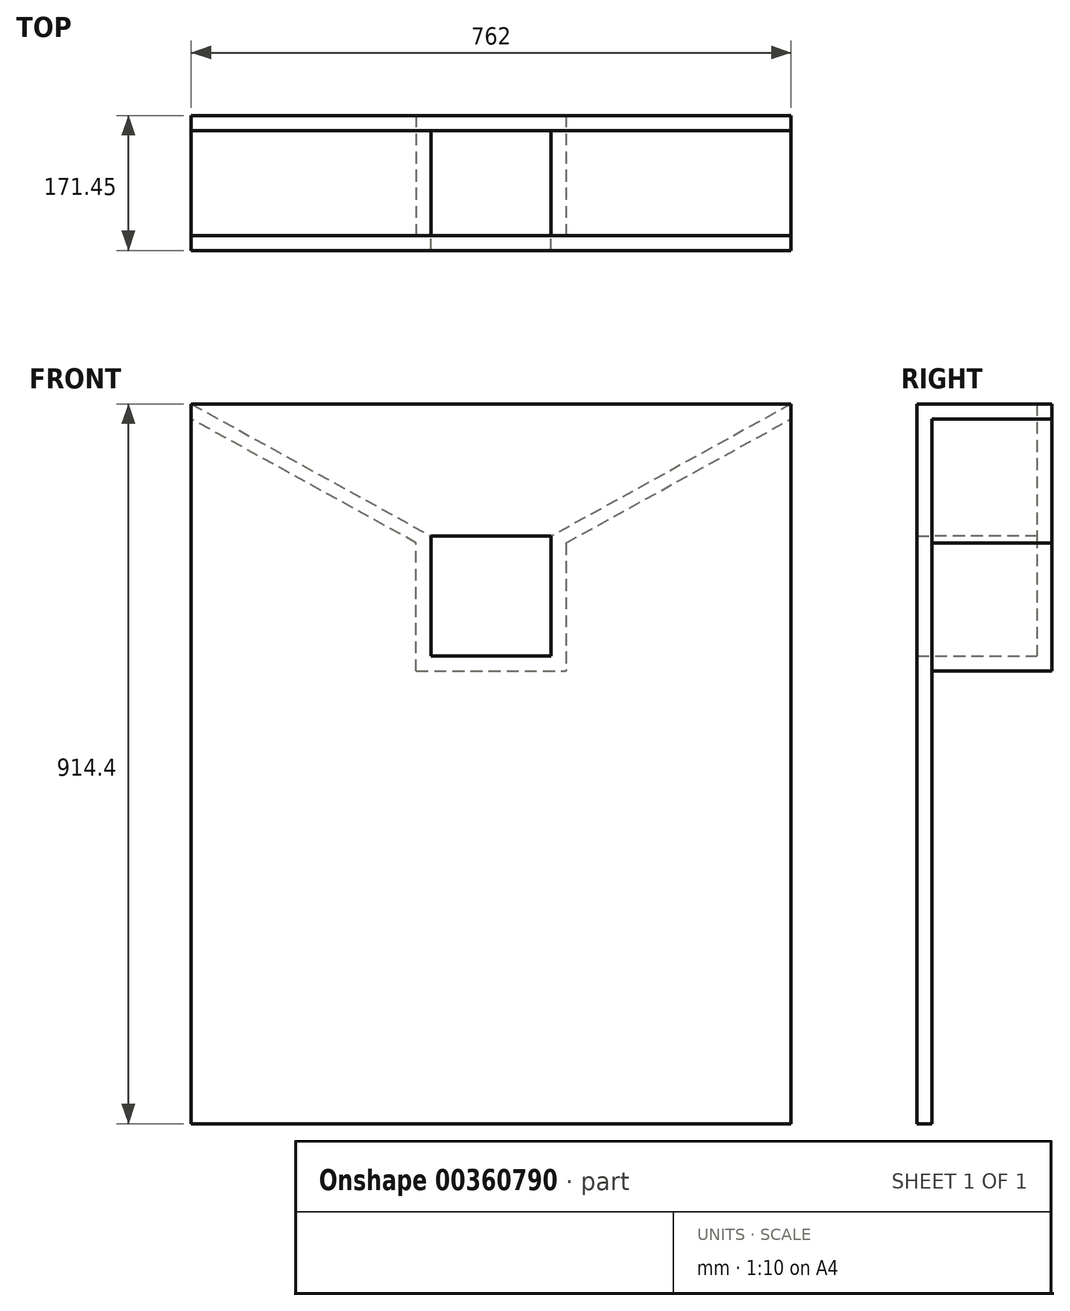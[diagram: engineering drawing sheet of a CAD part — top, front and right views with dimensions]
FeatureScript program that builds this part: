
annotation { "Feature Type Name" : "Feature", "Feature Type Description" : "" }
export const myFeature = defineFeature(function(context is Context, id is Id, definition is map)
    precondition{}
    {
        {
            var Q0;
            Q0=qCreatedBy(makeId("Front.planeOp"),FACE);
            var sketch = newSketch(context, id + "F0", { "sketchPlane" : qUnion([Q0])});
            skLineSegment(sketch, "E0.bottom", {"start": v(0, 0) * mm, "end": v(-762, 0) * mm});
            skLineSegment(sketch, "E0.top", {"start": v(0, 914.4) * mm, "end": v(-762, 914.4) * mm});
            skLineSegment(sketch, "E0.left", {"start": v(0, 0) * mm, "end": v(0, 914.4) * mm});
            skLineSegment(sketch, "E0.right", {"start": v(-762, 0) * mm, "end": v(-762, 914.4) * mm});
            skLineSegment(sketch, "E1.bottom", {"start": v(-304.8, 746.23) * mm, "end": v(-457.2, 746.23) * mm});
            skLineSegment(sketch, "E1.top", {"start": v(-304.8, 593.83) * mm, "end": v(-457.2, 593.83) * mm});
            skLineSegment(sketch, "E1.left", {"start": v(-304.8, 746.23) * mm, "end": v(-304.8, 593.83) * mm});
            skLineSegment(sketch, "E1.right", {"start": v(-457.2, 746.23) * mm, "end": v(-457.2, 593.83) * mm});
            skLineSegment(sketch, "E2", {"start": v(-762, 914.4) * mm, "end": v(-457.2, 746.23) * mm});
            skLineSegment(sketch, "E3", {"start": v(0, 914.4) * mm, "end": v(-304.8, 746.23) * mm});
            skLineSegment(sketch, "E4.bottom", {"start": v(-457.2, 593.83) * mm, "end": v(-304.8, 593.83) * mm});
            skLineSegment(sketch, "E4.top", {"start": v(-476.25, 574.78) * mm, "end": v(-285.75, 574.78) * mm});
            skLineSegment(sketch, "E4.left", {"start": v(-476.25, 593.83) * mm, "end": v(-476.25, 574.78) * mm});
            skLineSegment(sketch, "E4.right", {"start": v(-285.75, 593.83) * mm, "end": v(-285.75, 574.78) * mm});
            skLineSegment(sketch, "E5", {"start": v(-285.75, 593.83) * mm, "end": v(-285.75, 737.7) * mm});
            skLineSegment(sketch, "E6", {"start": v(-476.25, 593.83) * mm, "end": v(-476.25, 737.7) * mm});
            skLineSegment(sketch, "E7", {"start": v(-285.75, 737.7) * mm, "end": v(0, 895.35) * mm});
            skLineSegment(sketch, "E8", {"start": v(-476.25, 737.7) * mm, "end": v(-762, 895.35) * mm});
            skPoint(sketch, "E9.orphan", {"position": v(-476.25, 756.74) * mm});
            skSolve(sketch);
        }
        {
            var Q0;
            {var subQ1=sQuery(id+"F0.wireOp",EDGE,"E0.bottom");Q0=makeQuery(id+"F0.imprint","IMPRINT",FACE,{"disambiguationData":[TD([[makeQuery(id+"F0.imprint","IMPRINT",EDGE,{"derivedFrom":subQ1}),-1.0]])]});}
            var Q1;
            Q1=makeQuery(id+"F0.imprint","IMPRINT",FACE,{"disambiguationData":[TD([[makeQuery(id+"F0.imprint","IMPRINT",EDGE,{"derivedFrom":sQuery(id+"F0.wireOp",EDGE,"E0.top")}),1.0]])]});
            var Q2;
            Q2=makeQuery(id+"F0.imprint","IMPRINT",FACE,{"disambiguationData":[TD([[makeQuery(id+"F0.imprint","IMPRINT",EDGE,{"derivedFrom":sQuery(id+"F0.wireOp",EDGE,"E1.left")}),1.0]])]});
            extrude(context, id + "F1", {"entities" : qUnion([Q0, Q1, Q2]), "depth" : 19.05 * mm});
        }
        {
            var Q0;
            Q0=makeQuery(id+"F0.imprint","IMPRINT",FACE,{"disambiguationData":[TD([[makeQuery(id+"F0.imprint","IMPRINT",EDGE,{"derivedFrom":sQuery(id+"F0.wireOp",EDGE,"E1.left")}),1.0]])]});
            extrude(context, id + "F2", {"entities" : qUnion([Q0]), "operationType" : NewBodyOperationType.ADD, "oppositeDirection" : true, "depth" : 152.4 * mm});
        }
        {
            var Q0;
            Q0=makeQuery(id+"F2.opExtrude","CAP_FACE",FACE,{"disambiguationData":[OSD([sQuery(id+"F0.wireOp",EDGE,"E0.left"),sQuery(id+"F0.wireOp",EDGE,"E0.right"),sQuery(id+"F0.wireOp",EDGE,"E1.left"),sQuery(id+"F0.wireOp",EDGE,"E1.right"),sQuery(id+"F0.wireOp",EDGE,"E2"),sQuery(id+"F0.wireOp",EDGE,"E3"),sQuery(id+"F0.wireOp",EDGE,"E4.bottom"),sQuery(id+"F0.wireOp",EDGE,"E4.top"),sQuery(id+"F0.wireOp",EDGE,"E4.left"),sQuery(id+"F0.wireOp",EDGE,"E4.right"),sQuery(id+"F0.wireOp",EDGE,"E5"),sQuery(id+"F0.wireOp",EDGE,"E6"),sQuery(id+"F0.wireOp",EDGE,"E7"),sQuery(id+"F0.wireOp",EDGE,"E8")])],"isStart":false});
            var sketch = newSketch(context, id + "F3", { "sketchPlane" : qUnion([Q0])});
            skLineSegment(sketch, "E10", {"start": v(285.75, 574.78) * mm, "end": v(476.25, 574.78) * mm});
            skLineSegment(sketch, "E11", {"start": v(476.25, 574.78) * mm, "end": v(476.25, 737.7) * mm});
            skLineSegment(sketch, "E12", {"start": v(476.25, 737.7) * mm, "end": v(762, 895.35) * mm});
            skLineSegment(sketch, "E13", {"start": v(762, 895.35) * mm, "end": v(762, 914.4) * mm});
            skLineSegment(sketch, "E14", {"start": v(762, 914.4) * mm, "end": v(0, 914.4) * mm});
            skLineSegment(sketch, "E15", {"start": v(0, 914.4) * mm, "end": v(0, 895.35) * mm});
            skLineSegment(sketch, "E16", {"start": v(0, 895.35) * mm, "end": v(285.75, 737.7) * mm});
            skLineSegment(sketch, "E17", {"start": v(285.75, 737.7) * mm, "end": v(285.75, 574.78) * mm});
            skSolve(sketch);
        }
        {
            var Q0;
            Q0=makeQuery(id+"F3.imprint","IMPRINT",FACE,{"disambiguationData":[TD([[makeQuery(id+"F3.imprint","IMPRINT",EDGE,{"derivedFrom":sQuery(id+"F3.wireOp",EDGE,"E14")}),1.0]])]});
            extrude(context, id + "F4", {"entities" : qUnion([Q0]), "operationType" : NewBodyOperationType.ADD, "oppositeDirection" : true, "depth" : 19.05 * mm});
        }
    });
